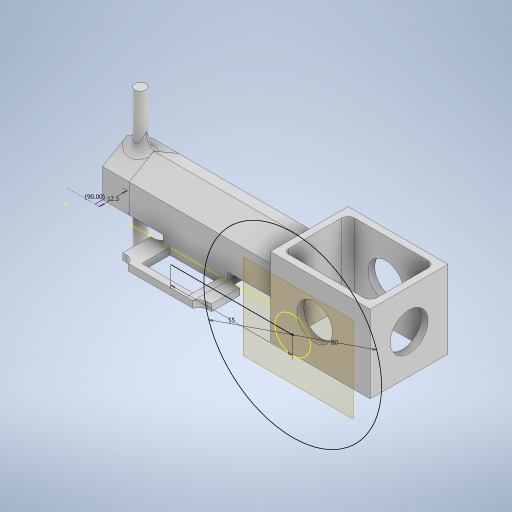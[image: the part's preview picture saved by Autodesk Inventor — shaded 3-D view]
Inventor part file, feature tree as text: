
AUTODESK INVENTOR PART (.ipt)
format: ipt  version: 2024 (Build 280153000, 153)  size: 569,344 bytes
history: native  units: in
note: dims shown in document units (in); Inventor stores cm internally (conversion verified against a paired STEP export)
features: sketch x17, extrude x14, fillet x6, plane x1
ambient origin geometry x8: Origin, YZ Plane, XZ Plane, XY Plane, X Axis, Y Axis, Z Axis, Center Point
bodies: Solid1 (feature_tree)
feature tree (38):
  extrude  "Extrusion1"  Depth=0.3937in
  extrude  "Extrusion2"  Depth=0.3937in TaperAngle=0.0deg
  extrude  "Extrusion3"  Depth=0.3937in TaperAngle=0.0deg
  extrude  "Extrusion4"  Depth=0.1969in
  fillet  "Fillet1"  Radius=2.7559in
  fillet  "Fillet2"  Radius=0.1969in
  extrude  "Extrusion5"  Depth=0.1575in
  extrude  "Extrusion6"  Depth=1.378in
  extrude  "Extrusion7"  Depth=1.7717in TaperAngle=0.0deg
  extrude  "Extrusion8"  Depth=0.1181in
  extrude  "Extrusion9"  Depth=0.1181in TaperAngle=0.0deg
  fillet  "Fillet3"  Radius=0.6693in
  fillet  "Fillet4"  Radius=0.1181in
  plane  "Work Plane1"
  sketch  "Sketch11"  dims[d30=0.9843in d31=0.6299in]
  extrude  "Extrusion10"  Depth=0.6299in
  sketch  "Sketch13"  dims[d35=0.0787in d36=0.3937in]
  extrude  "Extrusion11"  Depth=0.1181in
  extrude  "Extrusion12"  Depth=0.3937in
  sketch  "Sketch16"  dims[d43=0.9055in]
  extrude  "Extrusion13"  Depth=2.1654in
  fillet  "Fillet5"  Radius=2.1654in
  fillet  "Fillet6"  Radius=0.252in
  extrude  "Extrusion14"  TaperAngle=0.0deg  [1 undecoded]
  sketch  "Sketch1"  dims[d0=0.3937in d1=0.0984in]
  sketch  "Sketch2"  dims[d2=0.3937in d3=0.0in d4=0.0787in d5=0.0in]
  sketch  "Sketch3"  dims[d6=0.3937in d7=0.0787in d8=0.0in]
  sketch  "Sketch4"  dims[d9=0.2362in d10=0.1969in d11=2.7559in d12=0.0in d13=0.1969in]
  sketch  "Sketch5"  dims[d14=0.1575in d15=0.0984in]
  sketch  "Sketch6"  dims[d16=2.7559in d17=0.0in d18=1.378in]
  sketch  "Sketch8"  dims[d19=1.378in d20=1.7717in d21=0.0in]
  sketch  "Sketch9"  dims[d22=0.1181in d23=0.1181in]
  sketch  "Sketch10"  dims[d24=0.1181in d25=1.7717in d26=0.0in d27=0.6693in d28=0.1181in d29=0.0in]
  sketch  "Sketch12"  dims[d32=1.378in d33=0.0in d34=0.1181in]
  sketch  "Sketch14"  dims[d37=3.1496in d38=2.1654in d39=2.1654in d40=0.252in]
  sketch  "Sketch15"  dims[d41=0.2953in d42=0.0in]
  sketch  "Sketch17"  dims[d44=0.8661in]
  sketch  "Sketch18"  dims[d45=0.1929in d46=0.1181in d47=0.1181in d48=0.1181in d49=0.3642in d50=0.0in d51=0.4921in d52=90.0deg d53=0.6102in d54=0.0in d55=0.1181in d56=0.1181in d57=0.9055in d58=0.0in d59=1.1417in d60=0.2559in d61=0.0in d62=0.2461in d63=90.0deg d64=0.3346in d65=90.0deg d66=0.1181in d67=0.0in d68=0.1575in d69=0.1575in d70=0.3543in d71=0.0in]
note: 1 required parameter value undecoded (feature->parameter linkage not recoverable at this tier; creation-order binding heuristic only, values carry confidence <= 0.55)
